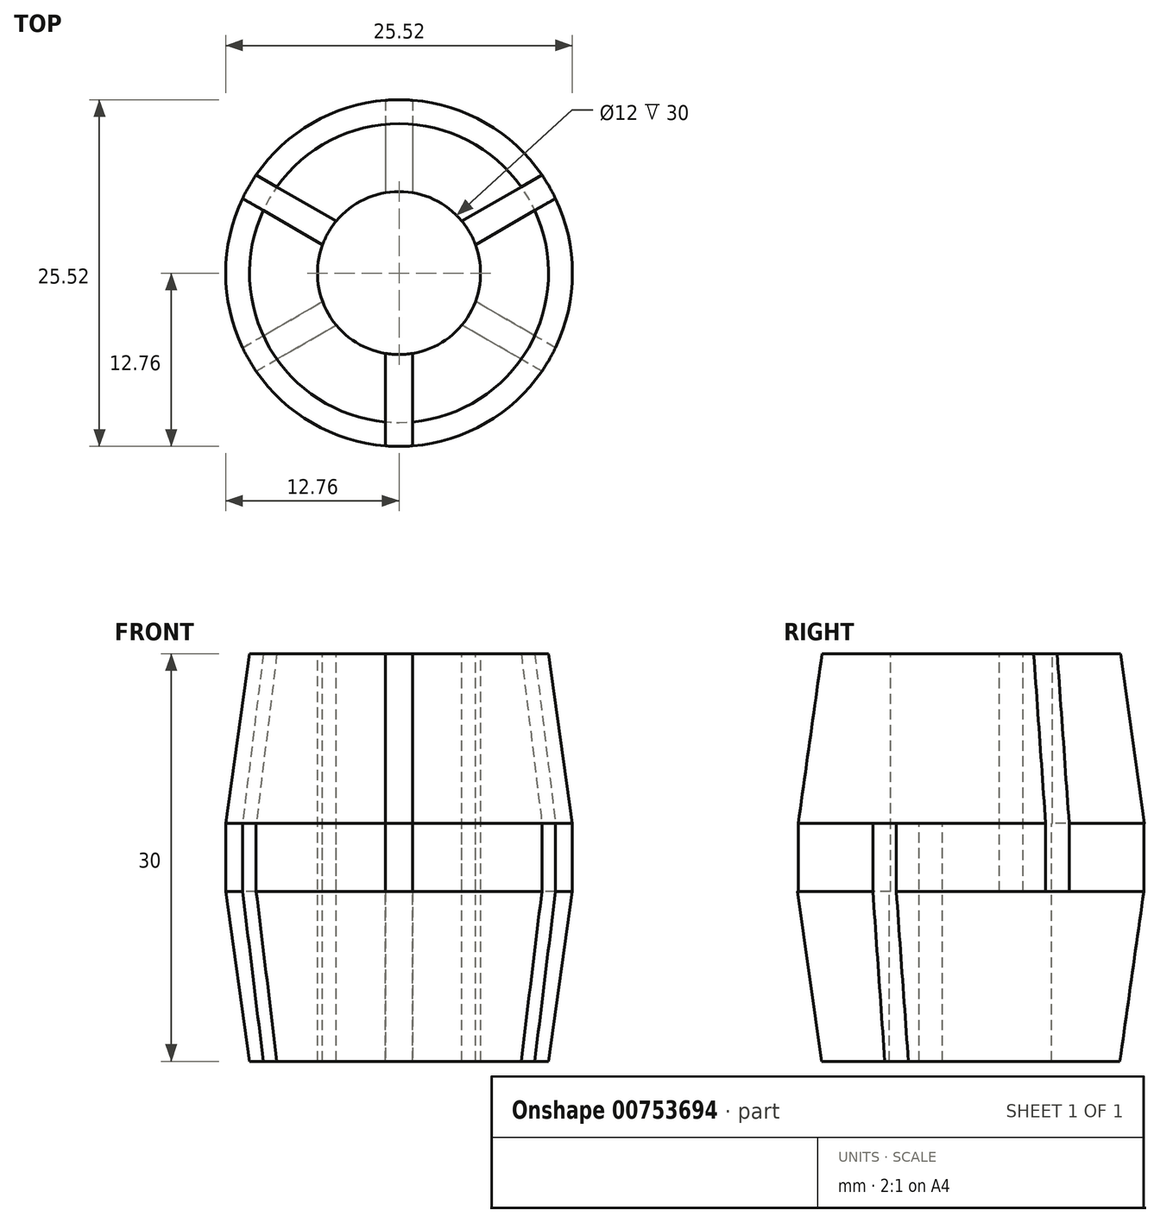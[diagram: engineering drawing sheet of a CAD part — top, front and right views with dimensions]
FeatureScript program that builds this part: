
annotation { "Feature Type Name" : "Feature", "Feature Type Description" : "" }
export const myFeature = defineFeature(function(context is Context, id is Id, definition is map)
    precondition{}
    {
        {
            var Q0;
            Q0=qCreatedBy(makeId("Front.planeOp"),FACE);
            var sketch = newSketch(context, id + "F0", { "sketchPlane" : qUnion([Q0])});
            skLineSegment(sketch, "E0", {"start": v(0, 35.95) * mm, "end": v(0, -42.4) * mm, "construction": true});
            skLineSegment(sketch, "E1", {"start": v(0, 0) * mm, "end": v(6, 0) * mm});
            skLineSegment(sketch, "E2", {"start": v(6, 0) * mm, "end": v(6, 30) * mm});
            skLineSegment(sketch, "E3", {"start": v(6, 30) * mm, "end": v(11, 30) * mm});
            skLineSegment(sketch, "E4", {"start": v(11, 30) * mm, "end": v(12.76, 17.5) * mm});
            skLineSegment(sketch, "E5", {"start": v(12.76, 17.5) * mm, "end": v(12.76, 12.5) * mm});
            skLineSegment(sketch, "E6", {"start": v(12.76, 12.5) * mm, "end": v(11, 0) * mm});
            skLineSegment(sketch, "E7", {"start": v(11, 0) * mm, "end": v(6, 0) * mm});
            skLineSegment(sketch, "E8", {"start": v(12.76, 17.5) * mm, "end": v(6, 17.5) * mm});
            skLineSegment(sketch, "E9", {"start": v(6, 12.5) * mm, "end": v(12.76, 12.5) * mm});
            skSolve(sketch);
        }
        {
            var Q0;
            Q0=makeQuery(id+"F0.imprint","IMPRINT",FACE,{"disambiguationData":[TD([[makeQuery(id+"F0.imprint","IMPRINT",EDGE,{"derivedFrom":sQuery(id+"F0.wireOp",EDGE,"E5")}),-1.0]])]});
            var Q1;
            Q1=sQuery(id+"F0.wireOp",EDGE,"E0");
            revolve(context, id + "F1", {"surfaceOperationType" : NewSurfaceOperationType.NEW, "entities" : qUnion([Q0]), "axis" : qUnion([Q1]), "revolveType" : RevolveType.FULL});
        }
        {
            var Q0;
            Q0=makeQuery(id+"F1.opRevolve","SWEPT_FACE",FACE,{"disambiguationData":[OSD([sQuery(id+"F0.wireOp",EDGE,"E8")])]});
            var sketch = newSketch(context, id + "F2", { "sketchPlane" : qUnion([Q0])});
            skLineSegment(sketch, "E10", {"start": v(0, 0) * mm, "end": v(0, 16.51) * mm, "construction": true});
            skLineSegment(sketch, "E11", {"start": v(-1, 12.72) * mm, "end": v(-1, 5.92) * mm});
            skLineSegment(sketch, "E12.MirrorCS", {"start": v(1, 12.72) * mm, "end": v(1, 5.92) * mm});
            skPoint(sketch, "E13.center", {"position": v(0, 0) * mm});
            skLineSegment(sketch, "E14.1.0", {"start": v(-11.51, 5.5) * mm, "end": v(-5.62, 2.1) * mm});
            skLineSegment(sketch, "E14.1.1", {"start": v(-10.51, 7.22) * mm, "end": v(-4.62, 3.82) * mm});
            skLineSegment(sketch, "E14.2.0", {"start": v(-10.51, -7.22) * mm, "end": v(-4.62, -3.82) * mm});
            skLineSegment(sketch, "E14.2.1", {"start": v(-11.51, -5.5) * mm, "end": v(-5.62, -2.1) * mm});
            skLineSegment(sketch, "E14.3.0", {"start": v(1, -12.72) * mm, "end": v(1, -5.92) * mm});
            skLineSegment(sketch, "E14.3.1", {"start": v(-1, -12.72) * mm, "end": v(-1, -5.92) * mm});
            skLineSegment(sketch, "E14.4.0", {"start": v(11.51, -5.5) * mm, "end": v(5.62, -2.1) * mm});
            skLineSegment(sketch, "E14.4.1", {"start": v(10.51, -7.22) * mm, "end": v(4.62, -3.82) * mm});
            skLineSegment(sketch, "E14.5.0", {"start": v(10.51, 7.22) * mm, "end": v(4.62, 3.82) * mm});
            skLineSegment(sketch, "E14.5.1", {"start": v(11.51, 5.5) * mm, "end": v(5.62, 2.1) * mm});
            skSolve(sketch);
        }
        {
            var Q0;
            {var subQ0=sQuery(id+"F2.wireOp",EDGE,"E13.1.0");Q0=makeQuery(id+"F2.imprint","IMPRINT",FACE,{"disambiguationData":[TD([[makeQuery(id+"F2.imprint","IMPRINT",EDGE,{"derivedFrom":subQ0}),-1.0]])]});}
            var Q1;
            {var subQ0=sQuery(id+"F2.wireOp",EDGE,"E13.2.0");Q1=makeQuery(id+"F2.imprint","IMPRINT",FACE,{"disambiguationData":[TD([[makeQuery(id+"F2.imprint","IMPRINT",EDGE,{"derivedFrom":subQ0}),-1.0]])]});}
            var Q2;
            {var subQ0=sQuery(id+"F2.wireOp",EDGE,"E11");Q2=makeQuery(id+"F2.imprint","IMPRINT",FACE,{"disambiguationData":[TD([[makeQuery(id+"F2.imprint","IMPRINT",EDGE,{"derivedFrom":subQ0}),1.0]])]});}
            var Q3;
            {var subQ0=sQuery(id+"F2.wireOp",EDGE,"E14.1.0");Q3=makeQuery(id+"F2.imprint","IMPRINT",FACE,{"disambiguationData":[TD([[makeQuery(id+"F2.imprint","IMPRINT",EDGE,{"derivedFrom":subQ0}),1.0]])]});}
            var Q4;
            {var subQ0=sQuery(id+"F2.wireOp",EDGE,"E14.2.0");Q4=makeQuery(id+"F2.imprint","IMPRINT",FACE,{"disambiguationData":[TD([[makeQuery(id+"F2.imprint","IMPRINT",EDGE,{"derivedFrom":subQ0}),1.0]])]});}
            var Q5;
            {var subQ0=sQuery(id+"F2.wireOp",EDGE,"E14.3.0");Q5=makeQuery(id+"F2.imprint","IMPRINT",FACE,{"disambiguationData":[TD([[makeQuery(id+"F2.imprint","IMPRINT",EDGE,{"derivedFrom":subQ0}),1.0]])]});}
            var Q6;
            {var subQ0=sQuery(id+"F2.wireOp",EDGE,"E14.4.0");Q6=makeQuery(id+"F2.imprint","IMPRINT",FACE,{"disambiguationData":[TD([[makeQuery(id+"F2.imprint","IMPRINT",EDGE,{"derivedFrom":subQ0}),1.0]])]});}
            var Q7;
            {var subQ0=sQuery(id+"F2.wireOp",EDGE,"E14.5.0");Q7=makeQuery(id+"F2.imprint","IMPRINT",FACE,{"disambiguationData":[TD([[makeQuery(id+"F2.imprint","IMPRINT",EDGE,{"derivedFrom":subQ0}),1.0]])]});}
            var Q8;
            Q8=makeQuery(id+"F4.opRevolve","SWEPT_FACE",FACE,{"disambiguationData":[OSD([sQuery(id+"F0.wireOp",EDGE,"E7")])]});
            extrude(context, id + "F3", {"entities" : qUnion([Q0, Q1, Q2, Q3, Q4, Q5, Q6, Q7]), "operationType" : NewBodyOperationType.REMOVE, "endBound" : BoundingType.UP_TO_NEXT, "oppositeDirection" : true, "depth" : 25 * mm, "endBoundEntityFace" : qUnion([Q8]), "offsetDistance" : 25 * mm});
        }
        {
            var Q0;
            {var subQ0=sQuery(id+"F0.wireOp",EDGE,"E3");Q0=makeQuery(id+"F0.imprint","IMPRINT",FACE,{"disambiguationData":[TD([[makeQuery(id+"F0.imprint","IMPRINT",EDGE,{"derivedFrom":subQ0}),-1.0]])]});}
            var Q1;
            Q1=makeQuery(id+"F0.imprint","IMPRINT",FACE,{"disambiguationData":[TD([[makeQuery(id+"F0.imprint","IMPRINT",EDGE,{"derivedFrom":sQuery(id+"F0.wireOp",EDGE,"E6")}),-1.0]])]});
            var Q2;
            Q2=sQuery(id+"F0.wireOp",EDGE,"E0");
            revolve(context, id + "F4", {"surfaceOperationType" : NewSurfaceOperationType.NEW, "entities" : qUnion([Q0, Q1]), "axis" : qUnion([Q2]), "revolveType" : RevolveType.FULL});
        }
        {
            var Q0;
            Q0=makeQuery(id+"F3.boolean.opBoolean","SPLIT",BODY,{"disambiguationData":[OD(0.0)],"derivedFrom":makeQuery(id+"F1.opRevolve","SWEPT_BODY",BODY,{"disambiguationData":[OSD([sQuery(id+"F0.wireOp",EDGE,"E2"),sQuery(id+"F0.wireOp",EDGE,"E5"),sQuery(id+"F0.wireOp",EDGE,"E8"),sQuery(id+"F0.wireOp",EDGE,"E9")])]})});
            var Q1;
            Q1=makeQuery(id+"F3.boolean.opBoolean","SPLIT",BODY,{"disambiguationData":[OD(1.0)],"derivedFrom":makeQuery(id+"F1.opRevolve","SWEPT_BODY",BODY,{"disambiguationData":[OSD([sQuery(id+"F0.wireOp",EDGE,"E2"),sQuery(id+"F0.wireOp",EDGE,"E5"),sQuery(id+"F0.wireOp",EDGE,"E8"),sQuery(id+"F0.wireOp",EDGE,"E9")])]})});
            var Q2;
            Q2=makeQuery(id+"F3.boolean.opBoolean","SPLIT",BODY,{"disambiguationData":[OD(2.0)],"derivedFrom":makeQuery(id+"F1.opRevolve","SWEPT_BODY",BODY,{"disambiguationData":[OSD([sQuery(id+"F0.wireOp",EDGE,"E2"),sQuery(id+"F0.wireOp",EDGE,"E5"),sQuery(id+"F0.wireOp",EDGE,"E8"),sQuery(id+"F0.wireOp",EDGE,"E9")])]})});
            var Q3;
            Q3=makeQuery(id+"F3.boolean.opBoolean","SPLIT",BODY,{"disambiguationData":[OD(3.0)],"derivedFrom":makeQuery(id+"F1.opRevolve","SWEPT_BODY",BODY,{"disambiguationData":[OSD([sQuery(id+"F0.wireOp",EDGE,"E2"),sQuery(id+"F0.wireOp",EDGE,"E5"),sQuery(id+"F0.wireOp",EDGE,"E8"),sQuery(id+"F0.wireOp",EDGE,"E9")])]})});
            var Q4;
            Q4=makeQuery(id+"F3.boolean.opBoolean","SPLIT",BODY,{"disambiguationData":[OD(4.0)],"derivedFrom":makeQuery(id+"F1.opRevolve","SWEPT_BODY",BODY,{"disambiguationData":[OSD([sQuery(id+"F0.wireOp",EDGE,"E2"),sQuery(id+"F0.wireOp",EDGE,"E5"),sQuery(id+"F0.wireOp",EDGE,"E8"),sQuery(id+"F0.wireOp",EDGE,"E9")])]})});
            var Q5;
            Q5=makeQuery(id+"F3.boolean.opBoolean","SPLIT",BODY,{"disambiguationData":[OD(5.0)],"derivedFrom":makeQuery(id+"F1.opRevolve","SWEPT_BODY",BODY,{"disambiguationData":[OSD([sQuery(id+"F0.wireOp",EDGE,"E2"),sQuery(id+"F0.wireOp",EDGE,"E5"),sQuery(id+"F0.wireOp",EDGE,"E8"),sQuery(id+"F0.wireOp",EDGE,"E9")])]})});
            var Q6;
            Q6=makeQuery(id+"F4.opRevolve","SWEPT_BODY",BODY,{"disambiguationData":[OSD([sQuery(id+"F0.wireOp",EDGE,"E2"),sQuery(id+"F0.wireOp",EDGE,"E6"),sQuery(id+"F0.wireOp",EDGE,"E7"),sQuery(id+"F0.wireOp",EDGE,"E9")])]});
            var Q7;
            Q7=makeQuery(id+"F4.opRevolve","SWEPT_BODY",BODY,{"disambiguationData":[OSD([sQuery(id+"F0.wireOp",EDGE,"E2"),sQuery(id+"F0.wireOp",EDGE,"E3"),sQuery(id+"F0.wireOp",EDGE,"E4"),sQuery(id+"F0.wireOp",EDGE,"E8")])]});
            booleanBodies(context, id + "F5", {"operationType" : BooleanOperationType.UNION, "tools" : qUnion([Q0, Q1, Q2, Q3, Q4, Q5, Q6, Q7])});
        }
        {
            var Q0;
            {var subQ1=sQuery(id+"F0.wireOp",EDGE,"E8");Q0=makeQuery(id+"F5.opBoolean","SPLIT",FACE,{"disambiguationData":[TD([makeQuery(id+"F3.boolean.opBoolean","COPY",FACE,{"derivedFrom":makeQuery(id+"F3.opExtrude","SWEPT_FACE",FACE,{"disambiguationData":[OSD([sQuery(id+"F2.wireOp",EDGE,"E14.3.0")])]})})])],"derivedFrom":makeQuery(id+"F4.opRevolve","SWEPT_FACE",FACE,{"disambiguationData":[OSD([subQ1])]})});}
            var Q1;
            {var subQ1=sQuery(id+"F0.wireOp",EDGE,"E8");Q1=makeQuery(id+"F5.opBoolean","SPLIT",FACE,{"disambiguationData":[TD([makeQuery(id+"F3.boolean.opBoolean","COPY",FACE,{"derivedFrom":makeQuery(id+"F3.opExtrude","SWEPT_FACE",FACE,{"disambiguationData":[OSD([sQuery(id+"F2.wireOp",EDGE,"E14.5.0")])]})})])],"derivedFrom":makeQuery(id+"F4.opRevolve","SWEPT_FACE",FACE,{"disambiguationData":[OSD([subQ1])]})});}
            var Q2;
            {var subQ1=sQuery(id+"F0.wireOp",EDGE,"E8");Q2=makeQuery(id+"F5.opBoolean","SPLIT",FACE,{"disambiguationData":[TD([makeQuery(id+"F3.boolean.opBoolean","COPY",FACE,{"derivedFrom":makeQuery(id+"F3.opExtrude","SWEPT_FACE",FACE,{"disambiguationData":[OSD([sQuery(id+"F2.wireOp",EDGE,"E14.1.0")])]})})])],"derivedFrom":makeQuery(id+"F4.opRevolve","SWEPT_FACE",FACE,{"disambiguationData":[OSD([subQ1])]})});}
            extrude(context, id + "F6", {"entities" : qUnion([Q0, Q1, Q2]), "operationType" : NewBodyOperationType.REMOVE, "oppositeDirection" : true, "depth" : 25 * mm, "offsetDistance" : 25 * mm});
        }
        {
            var Q0;
            {var subQ1=sQuery(id+"F0.wireOp",EDGE,"E9");Q0=makeQuery(id+"F5.opBoolean","SPLIT",FACE,{"disambiguationData":[TD([makeQuery(id+"F3.boolean.opBoolean","COPY",FACE,{"derivedFrom":makeQuery(id+"F3.opExtrude","SWEPT_FACE",FACE,{"disambiguationData":[OSD([sQuery(id+"F2.wireOp",EDGE,"E14.4.0")])]})})])],"derivedFrom":makeQuery(id+"F4.opRevolve","SWEPT_FACE",FACE,{"disambiguationData":[OSD([subQ1])]})});}
            var Q1;
            {var subQ1=sQuery(id+"F0.wireOp",EDGE,"E9");Q1=makeQuery(id+"F5.opBoolean","SPLIT",FACE,{"disambiguationData":[TD([makeQuery(id+"F3.boolean.opBoolean","COPY",FACE,{"derivedFrom":makeQuery(id+"F3.opExtrude","SWEPT_FACE",FACE,{"disambiguationData":[OSD([sQuery(id+"F2.wireOp",EDGE,"E11")])]})})])],"derivedFrom":makeQuery(id+"F4.opRevolve","SWEPT_FACE",FACE,{"disambiguationData":[OSD([subQ1])]})});}
            var Q2;
            {var subQ1=sQuery(id+"F0.wireOp",EDGE,"E9");Q2=makeQuery(id+"F5.opBoolean","SPLIT",FACE,{"disambiguationData":[TD([makeQuery(id+"F3.boolean.opBoolean","COPY",FACE,{"derivedFrom":makeQuery(id+"F3.opExtrude","SWEPT_FACE",FACE,{"disambiguationData":[OSD([sQuery(id+"F2.wireOp",EDGE,"E14.2.0")])]})})])],"derivedFrom":makeQuery(id+"F4.opRevolve","SWEPT_FACE",FACE,{"disambiguationData":[OSD([subQ1])]})});}
            extrude(context, id + "F7", {"entities" : qUnion([Q0, Q1, Q2]), "operationType" : NewBodyOperationType.REMOVE, "oppositeDirection" : true, "depth" : 25 * mm, "offsetDistance" : 25 * mm});
        }
    });
